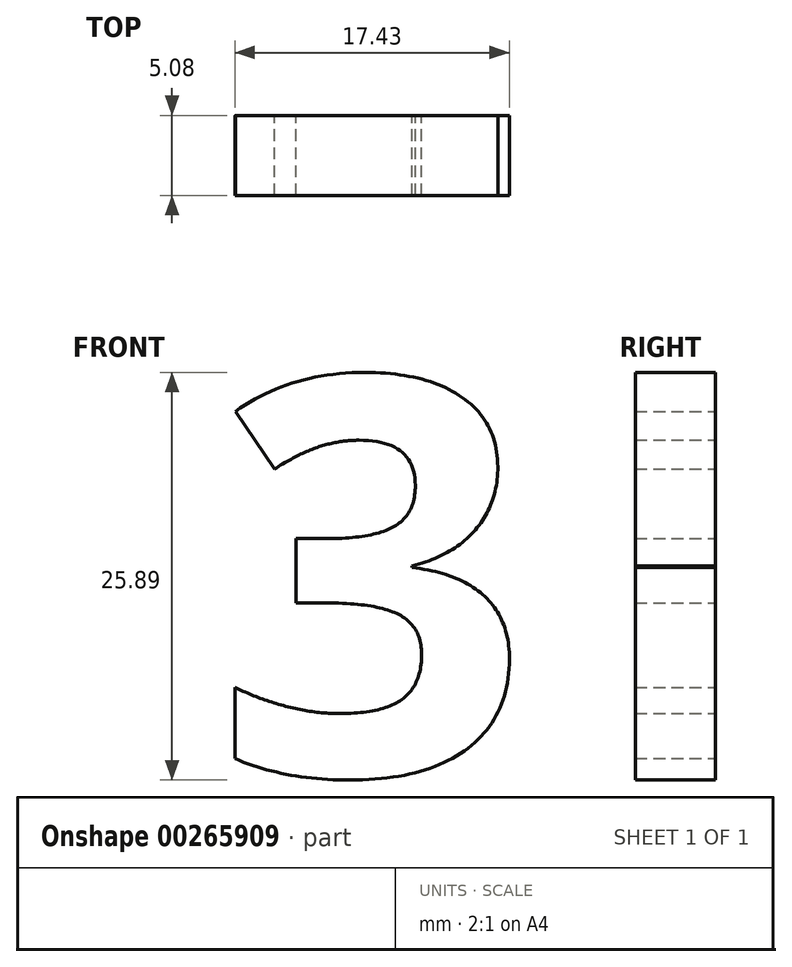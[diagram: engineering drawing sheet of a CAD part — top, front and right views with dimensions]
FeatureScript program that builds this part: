
annotation { "Feature Type Name" : "Feature", "Feature Type Description" : "" }
export const myFeature = defineFeature(function(context is Context, id is Id, definition is map)
    precondition{}
    {
        {
            var Q0;
            Q0=qCreatedBy(makeId("Front.planeOp"),FACE);
            var sketch = newSketch(context, id + "F0", { "sketchPlane" : qUnion([Q0])});
            skText(sketch, "E0", { "text": "3", "fontName": "OpenSans-Bold.ttf"});
            const initialGuessF0  = {"E0": [-0.01495, 0.00254, 1, 0, 0.0254]};
            skSetInitialGuess(sketch, initialGuessF0);
            skSolve(sketch);
        }
        {
            var Q0;
            Q0 = qSketchRegion(id + "F0", true);
            extrude(context, id + "F1", {"entities" : qUnion([Q0]), "depth" : 5.08 * mm});
        }
    });
